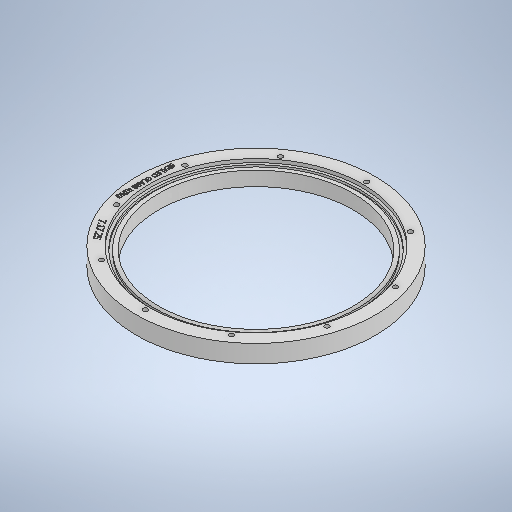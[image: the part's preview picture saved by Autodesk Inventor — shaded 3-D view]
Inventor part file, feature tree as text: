
AUTODESK INVENTOR PART (.ipt)
format: ipt  version: 2025 (Build 290162000, 162)  size: 716,800 bytes
history: native  units: mm
features: sketch x6, extrude x3, emboss x2, hole x1, pattern_circular x1
ambient origin geometry x8: Origin, YZ Plane, XZ Plane, XY Plane, X Axis, Y Axis, Z Axis, Center Point
bodies: Solid1 (feature_tree)
feature tree (13):
  extrude  "Ring"  Depth=270.0mm
  extrude  "Glass Seat"  Depth=241.0mm
  hole  "Holes"  [1 undecoded]
  pattern_circular  "Circular Pattern1"  Count=10 Angle=360.0deg
  emboss  "Emboss1"
  extrude  "Seal Groove"  Depth=2.5mm TaperAngle=0.0deg
  emboss  "Emboss2"
  sketch  "Sketch1"  dims[d0=220.0mm d1=270.0mm]
  sketch  "Sketch2"  dims[d2=20.0mm d3=0.0mm d4=241.0mm]
  sketch  "Sketch3"  dims[d5=3.9mm d6=0.0mm]
  sketch  "Sketch4"  dims[d7=5.2mm d8=6.0mm d9=4.0mm d10=2.0mm d11=90.0deg d12=8.0mm d13=20.594885mm d14=125.0mm d15=100.0mm d16=360.0deg]
  sketch  "Sketch5"  dims[d18=1.0mm d19=0.0mm d23=2.5mm d24=0.0mm]
  sketch  "Sketch6"  dims[d25=3.0mm d26=3.0mm d27=1.0mm d28=0.0mm]
note: 1 required parameter value undecoded (feature->parameter linkage not recoverable at this tier; creation-order binding heuristic only, values carry confidence <= 0.55)
